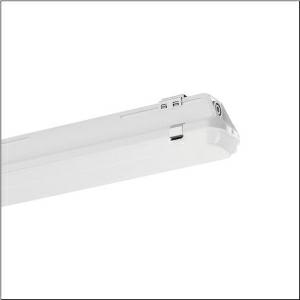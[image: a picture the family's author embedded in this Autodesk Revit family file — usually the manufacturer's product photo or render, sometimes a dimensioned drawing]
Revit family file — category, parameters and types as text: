
# Revit family: monsun_r__12_51fp108p460h_5576
name_source: partatom
category: Lighting Fixtures
units: mm (PartAtom-declared; Revit-internal decimal feet)

## family parameters
Cut with Voids When Loaded = No
Host = Face
Light Source = No
Part Type = Normal
Room Calculation Point = No
Round Connector Dimension = Use Diameter
Shared = No

## types (1)
- Monsun® 12 (1 x LED, 6100 lm, 33.9 W, 4000K)
    Apparent Load = 34 VA
    CIE Flux Codes = 47 77 93 94 100
    Color Rendering = 80
    Color Temperature = 4000K
    Default Elevation = 1800 mm
    Description = Monsun® 12, damp-proof luminaire, chain hanger, primary optical cover: enclosure, of PMMA, light emission: direct distribution, primary light characteristic: symmetric, installation type: suspended mounting, surface-mounted, horizontal mounting, vertical mounting, LED rated luminous flux: 6.100 lm, light colour: 840, colour temperature: 4000K, control gear: ECG, with terminal, 3-pole, max. 2.5mm², mains connection: 220..240V, AC, 50/60Hz, rated input power: 34W, luminaire housing, of glass-fibre reinforced polyester, uncoated, bright grey, length: 1.590 mm, width: 90 mm, height: 88mm, clip for enclosure, of stainless steel (V2A), ceiling mounting element, of stainless steel (V2A), chain hanger, of stainless steel (V2A), protection rating (complete): IP66, insulation class (complete): insulation class I (protective earthing), certification: CE, ENEC, VDE, protection symbol: D, impact resistance: IK04, permissible ambient temperature for indoor applications: -35..+40°C, standard: EN 50419, EN 60598-2-1, no direct snow, no direct sun, no direct rain, for indoor or canopied outdoor use, corresponds to IFS (International Featured Standards) requirements for safety and quality in the food industry, for animal farming (ammonia tested): for use in cowhouse, pig house, horse-stables... (not for use in poultry stables), AT max for animal farming = 40°C, packaging unit: 1 piece
    Height = 89 mm
    Lamp = 1 x LED
    Lamp Light Flux = 6100 lm
    Lamp Power = 33.9 W
    Lamp count = 1
    Length = 1590 mm
    Luminous efficacy = 180 lm/W
    Manufacturer = Siteco
    ModVariant = No
    Model = 51FP108P460H
    Mounting Place = Ceiling
    Mounting Type = Pendant
    Number of Poles = 1
    OnlyDefault = Yes
    Power Factor = 1
    Product Name = Monsun® 12
    Product group = damp-proof luminaire | ceiling pendant
    ProductGroupID = 908
    Protection Class = Protection class I
    Protection Degree = IP 66
    RLX_Detail_Level = 1
    RlxData = <blob elided: 88297 chars, md5=7db27590>
    Socket = socket
    Standby Power = 0 W
    System Light Flux = 6100 lm
    System Power = 34 W
    Type Comments = Product without accessories
    Type Image = l_1004748.jpg
    URL = http://relux.com
    VarID = ---
    Voltage = 0 V
    Weight = 0.00 kg
    Width = 90 mm

## geometry (parser evidence)
native form markers: Blend x4, Sweep x13
no freeform markers — native parametric forms only
